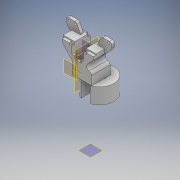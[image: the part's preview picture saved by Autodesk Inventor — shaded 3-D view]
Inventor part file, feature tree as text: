
AUTODESK INVENTOR PART (.ipt)
format: ipt  version: 2018 (Build 220112000, 112)  size: 587,264 bytes
history: native  units: mm
features: extrude x26, sketch x23, plane x6, mirror x5, fillet x2
ambient origin geometry x8: Origin, YZ Plane, XZ Plane, XY Plane, X Axis, Y Axis, Z Axis, Center Point
bodies: Solid1 (feature_tree)
feature tree (62):
  extrude  "base"  Depth=32.0mm
  extrude  "servo_place"  Depth=25.0mm
  plane  "Work Plane1"
  extrude  "pilars_top"  Depth=6.25mm
  extrude  "base_top"  Depth=12.5mm
  extrude  "screw_hole"  Depth=15.0mm TaperAngle=0.0deg
  plane  "Work Plane2"
  plane  "Work Plane6"
  plane  "Work Plane5"
  extrude  "Extrusion16"  Depth=18.0mm
  plane  "Work Plane3"
  plane  "Work Plane4"
  mirror  "Mirror1"
  mirror  "Mirror2"
  extrude  "Extrusion18"  Depth=5.0mm TaperAngle=0.0deg
  extrude  "Extrusion19"  Depth=2.5mm
  extrude  "Extrusion20"  Depth=5.0mm
  mirror  "Mirror3"
  mirror  "Mirror4"
  extrude  "Extrusion21"  Depth=25.0mm
  extrude  "Extrusion22"  [1 undecoded]
  extrude  "Extrusion23"  Depth=5.0mm
  extrude  "Extrusion11"  Depth=20.0mm
  extrude  "Extrusion24"  Depth=5.0mm
  fillet  "Fillet5"  Radius=30.0mm
  mirror  "Mirror5"
  extrude  "Extrusion25"  Depth=2.5mm
  extrude  "Extrusion26"  Depth=2.5mm
  extrude  "Extrusion27"  Depth=12.5mm
  fillet  "Fillet6"  Radius=12.5mm
  extrude  "Extrusion28"  Depth=12.5mm
  extrude  "Extrusion29"  Depth=7.0mm
  extrude  "Extrusion32"  Depth=27.0mm
  extrude  "Extrusion33"  Depth=10.0mm TaperAngle=0.0deg
  extrude  "Extrusion34"  Depth=3.5mm
  extrude  "Extrusion35"  Depth=3.5mm
  extrude  "Extrusion36"  Depth=3.0mm
  extrude  "Extrusion37"  Depth=15.0mm
  extrude  "Extrusion38"  Depth=12.0mm
  sketch  "Sketch1"  dims[d0=18.0mm d1=32.0mm]
  sketch  "Sketch2"  dims[d2=25.0mm d3=0.0mm d4=11.5mm]
  sketch  "Sketch6"  dims[d5=90.0deg d6=6.25mm]
  sketch  "Sketch9"  dims[d7=23.0mm d8=12.5mm]
  sketch  "Sketch18"  dims[d9=18.0mm d10=0.0mm d26=15.0mm d27=0.0mm]
  sketch  "Sketch19"  dims[d39=18.0mm d40=18.0mm]
  sketch  "Sketch20"  dims[d41=5.0mm d42=0.0mm d47=5.0mm d48=0.0mm]
  sketch  "Sketch21"  dims[d55=5.0mm d56=0.0mm d60=2.5mm]
  sketch  "Sketch22"  dims[d61=5.0mm d62=5.0mm]
  sketch  "Sketch23"  dims[d63=-10.0mm d95=25.0mm]
  sketch  "Sketch24"  dims[d96=4.6mm d97=0.0mm d98=-16.0mm]
  sketch  "Sketch25"  dims[d100=12.5mm d105=5.0mm]
  sketch  "Sketch26"  dims[d106=10.0mm d107=20.0mm]
  sketch  "Sketch27"  dims[d108=10.0mm d109=0.0mm d110=5.0mm d111=30.0mm]
  sketch  "Sketch28"  dims[d112=3.0mm d113=0.0mm d114=2.5mm]
  sketch  "Sketch29"  dims[d115=2.5mm d116=2.8mm]
  sketch  "Sketch32"  dims[d117=5.0mm d118=0.0mm d119=11.75mm d120=12.5mm]
  sketch  "Sketch33"  dims[d121=23.5mm d122=12.5mm]
  sketch  "Sketch34"  dims[d123=10.0mm d124=0.0mm d125=7.0mm]
  sketch  "Sketch35"  dims[d126=10.0mm d127=0.0mm d131=27.0mm]
  sketch  "Sketch36"  dims[d132=27.0mm d133=10.0mm d134=0.0mm]
  sketch  "Sketch37"  dims[d135=10.0mm d137=3.5mm]
  sketch  "Sketch38"  dims[d138=10.0mm d139=3.5mm d140=3.0mm d141=15.0mm d142=27.052603mm d143=1.0mm d144=18.0mm d145=8.0mm d146=6.0mm d147=5.0mm d148=0.0mm d149=4.0mm d150=11.5mm d151=23.0mm d152=5.0mm d153=0.0mm d154=15.0mm d155=0.0mm d156=3.0mm d157=12.5mm d158=12.5mm d159=90.0deg d160=25.0mm d161=90.0deg d162=12.5mm d163=18.0mm d164=0.0mm d165=5.0mm d166=1.8mm d167=90.0deg d168=2.0mm d169=1.8mm d170=90.0deg d171=2.0mm d172=18.0mm d173=0.0mm d174=7.0mm d175=18.0mm d176=0.0mm d177=7.5mm d178=90.0deg d179=50.0mm d180=55.0mm d187=90.0deg d190=7.5mm d191=90.0deg d192=19.4mm d193=50.0mm d194=18.0mm d195=0.0mm d196=24.4mm d197=50.0mm d198=9.0mm d199=0.0mm d200=2.5mm d201=3.5mm d202=0.0mm d203=7.0mm d204=2.0mm d205=2.0mm d206=9.0mm d207=0.0mm d208=2.5mm d209=3.5mm d210=7.0mm d211=2.0mm d212=2.0mm d213=9.0mm d214=0.0mm d215=10.0mm d216=0.0mm d217=22.0mm d218=4.0mm d219=0.0mm d221=35.4mm d222=15.0mm d223=32.968414mm d224=2.0mm d225=10.0mm d226=0.0mm d227=1.0mm d228=24.4mm d229=24.0mm d230=12.0mm]
note: 1 required parameter value undecoded (feature->parameter linkage not recoverable at this tier; creation-order binding heuristic only, values carry confidence <= 0.55)
